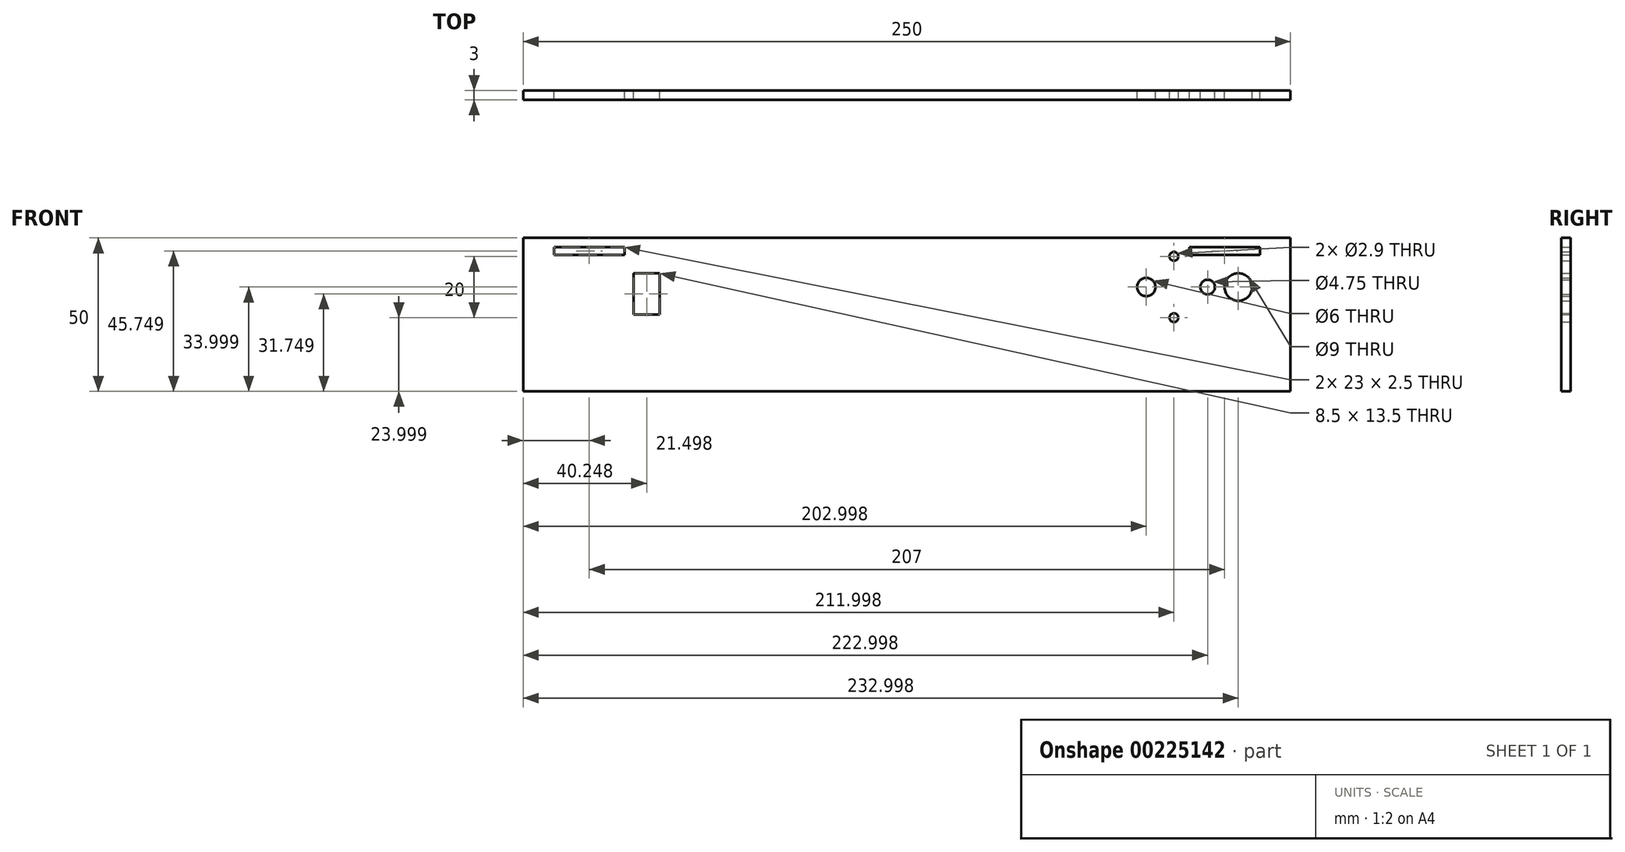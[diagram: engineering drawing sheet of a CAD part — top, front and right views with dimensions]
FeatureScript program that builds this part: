
annotation { "Feature Type Name" : "Feature", "Feature Type Description" : "" }
export const myFeature = defineFeature(function(context is Context, id is Id, definition is map)
    precondition{}
    {
        {
            var Q0;
            Q0=qCreatedBy(makeId("Front.planeOp"),FACE);
            var sketch = newSketch(context, id + "F0", { "sketchPlane" : qUnion([Q0])});
            skLineSegment(sketch, "E0.bottom", {"start": v(-167.72, 41.3) * mm, "end": v(82.28, 41.3) * mm});
            skLineSegment(sketch, "E0.top", {"start": v(-167.72, -8.7) * mm, "end": v(82.28, -8.7) * mm});
            skLineSegment(sketch, "E0.left", {"start": v(-167.72, 41.3) * mm, "end": v(-167.72, -8.7) * mm});
            skLineSegment(sketch, "E0.right", {"start": v(82.28, 41.3) * mm, "end": v(82.28, -8.7) * mm});
            skLineSegment(sketch, "E1.top", {"start": v(-157.72, 35.8) * mm, "end": v(-147.72, 35.8) * mm});
            skLineSegment(sketch, "E1.left", {"start": v(-157.72, 38.3) * mm, "end": v(-157.72, 35.8) * mm});
            skLineSegment(sketch, "E2.top", {"start": v(-144.72, 35.8) * mm, "end": v(-134.72, 35.8) * mm});
            skLineSegment(sketch, "E2.right", {"start": v(-134.72, 38.3) * mm, "end": v(-134.72, 35.8) * mm});
            skLineSegment(sketch, "E3.top", {"start": v(62.28, 38.3) * mm, "end": v(72.28, 38.3) * mm});
            skLineSegment(sketch, "E3.right", {"start": v(72.28, 35.8) * mm, "end": v(72.28, 38.3) * mm});
            skLineSegment(sketch, "E4.left", {"start": v(49.28, 38.3) * mm, "end": v(49.28, 35.8) * mm});
            skLineSegment(sketch, "E5.top", {"start": v(72.28, 35.8) * mm, "end": v(49.28, 35.8) * mm});
            skLineSegment(sketch, "E5.left", {"start": v(72.28, 38.3) * mm, "end": v(72.28, 35.8) * mm});
            skLineSegment(sketch, "E5.right", {"start": v(49.28, 35.8) * mm, "end": v(49.28, 13.3) * mm});
            skLineSegment(sketch, "E6", {"start": v(62.28, 38.3) * mm, "end": v(49.28, 38.3) * mm});
            skLineSegment(sketch, "E7.bottom", {"start": v(-134.72, 38.3) * mm, "end": v(-157.72, 38.3) * mm});
            skLineSegment(sketch, "E7.top", {"start": v(-134.72, 35.8) * mm, "end": v(-157.72, 35.8) * mm});
            skSolve(sketch);
        }
        {
            var Q0;
            Q0 = qSketchRegion(id + "F0", true);
            extrude(context, id + "F1", {"entities" : qUnion([Q0]), "depth" : 3 * mm});
        }
        {
            var Q0;
            Q0 = qSketchRegion(id + "F0", true);
            extrude(context, id + "F2", {"entities" : qUnion([Q0]), "operationType" : NewBodyOperationType.ADD, "depth" : 3 * mm});
        }
        {
            var Q0;
            Q0=makeQuery(id+"F1.opExtrude","CAP_FACE",FACE,{"disambiguationData":[OSD([sQuery(id+"F0.wireOp",EDGE,"E0.bottom"),sQuery(id+"F0.wireOp",EDGE,"E0.top"),sQuery(id+"F0.wireOp",EDGE,"E0.left"),sQuery(id+"F0.wireOp",EDGE,"E0.right"),sQuery(id+"F0.wireOp",EDGE,"E3.top"),sQuery(id+"F0.wireOp",EDGE,"E4.left"),sQuery(id+"F0.wireOp",EDGE,"E5.top"),sQuery(id+"F0.wireOp",EDGE,"E5.left"),sQuery(id+"F0.wireOp",EDGE,"E6"),sQuery(id+"F0.wireOp",EDGE,"E7.top"),sQuery(id+"F0.wireOp",EDGE,"E2.right"),sQuery(id+"F0.wireOp",EDGE,"E1.left"),sQuery(id+"F0.wireOp",EDGE,"E7.bottom")])],"isStart":true});
            var sketch = newSketch(context, id + "F3", { "sketchPlane" : qUnion([Q0])});
            skCircle(sketch, "E8", {"center": v(-65.28, 25.3) * mm, "radius": 4.5 * mm});
            skCircle(sketch, "E9", {"center": v(-44.28, 15.3) * mm, "radius": 1.45 * mm});
            skCircle(sketch, "E10", {"center": v(-44.28, 35.3) * mm, "radius": 1.45 * mm});
            skCircle(sketch, "E11", {"center": v(-55.28, 25.3) * mm, "radius": 2.38 * mm});
            skCircle(sketch, "E12", {"center": v(-35.28, 25.3) * mm, "radius": 3 * mm});
            skLineSegment(sketch, "E13.bottom", {"start": v(131.72, 29.8) * mm, "end": v(123.22, 29.8) * mm});
            skLineSegment(sketch, "E13.top", {"start": v(131.72, 16.3) * mm, "end": v(123.22, 16.3) * mm});
            skLineSegment(sketch, "E13.left", {"start": v(131.72, 29.8) * mm, "end": v(131.72, 16.3) * mm});
            skLineSegment(sketch, "E13.right", {"start": v(123.22, 29.8) * mm, "end": v(123.22, 16.3) * mm});
            skSolve(sketch);
        }
        {
            var Q0;
            Q0 = qSketchRegion(id + "F3", true);
            extrude(context, id + "F4", {"entities" : qUnion([Q0]), "operationType" : NewBodyOperationType.REMOVE, "oppositeDirection" : true, "depth" : 25 * mm});
        }
    });
